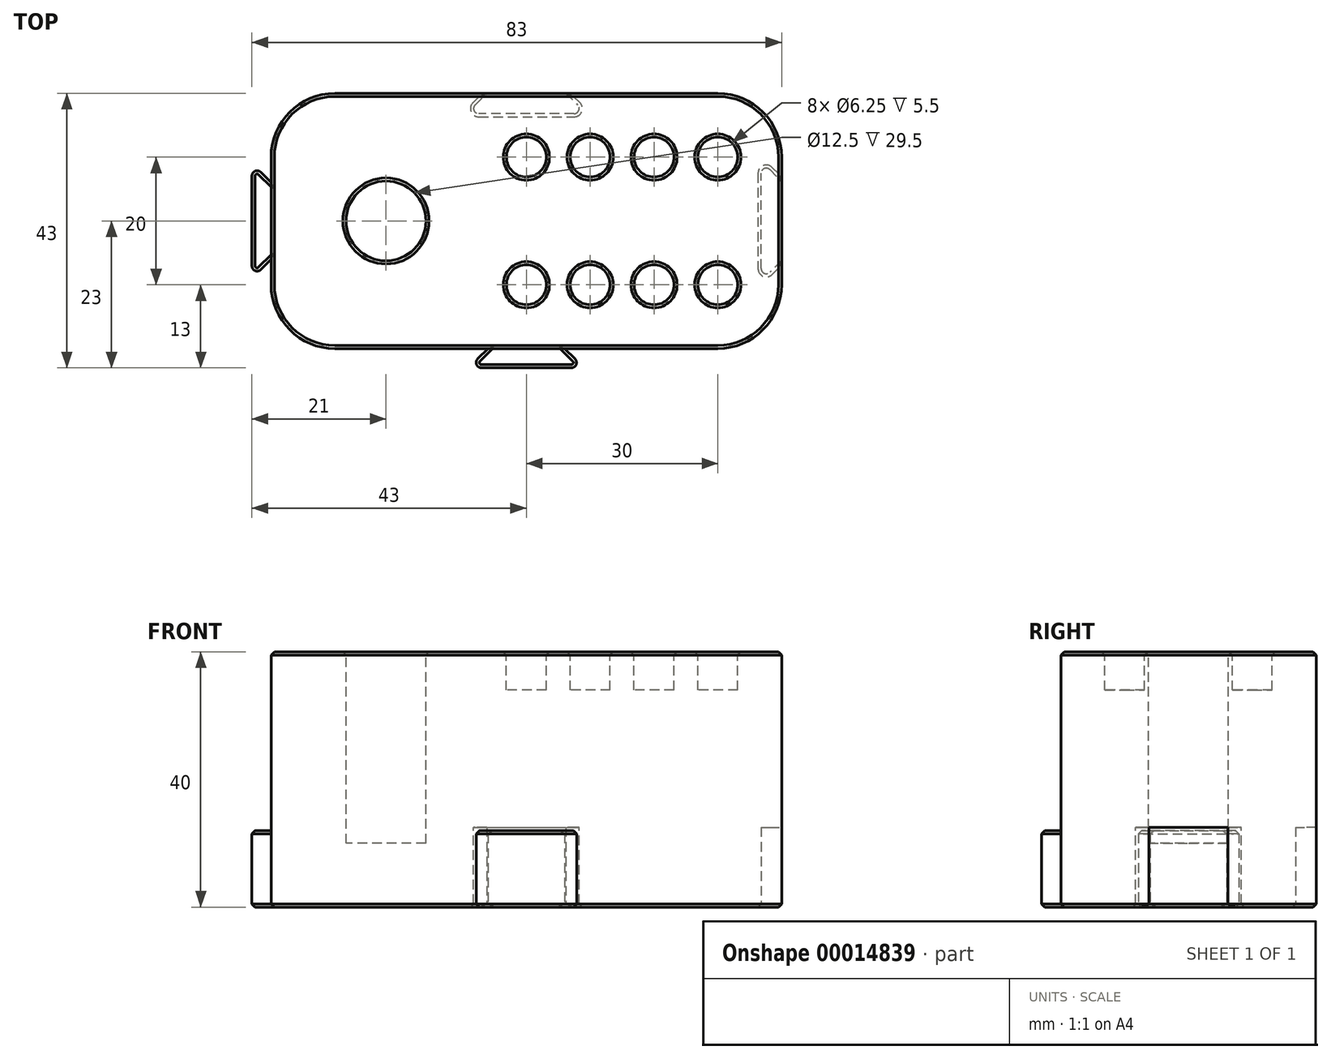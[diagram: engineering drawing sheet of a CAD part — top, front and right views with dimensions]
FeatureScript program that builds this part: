
annotation { "Feature Type Name" : "Feature", "Feature Type Description" : "" }
export const myFeature = defineFeature(function(context is Context, id is Id, definition is map)
    precondition{}
    {
        {
            var Q0;
            Q0=qCreatedBy(makeId("Top.planeOp"),FACE);
            var sketch = newSketch(context, id + "F0", { "sketchPlane" : qUnion([Q0])});
            skLineSegment(sketch, "E0.bottom", {"start": v(0, 0) * mm, "end": v(80, 0) * mm});
            skLineSegment(sketch, "E0.top", {"start": v(0, 40) * mm, "end": v(80, 40) * mm});
            skLineSegment(sketch, "E0.left", {"start": v(0, 0) * mm, "end": v(0, 40) * mm});
            skLineSegment(sketch, "E0.right", {"start": v(80, 0) * mm, "end": v(80, 40) * mm});
            skLineSegment(sketch, "E1", {"start": v(34, 0) * mm, "end": v(31, -3) * mm});
            skLineSegment(sketch, "E2", {"start": v(31, -3) * mm, "end": v(49, -3) * mm});
            skLineSegment(sketch, "E3", {"start": v(49, -3) * mm, "end": v(46, 0) * mm});
            skLineSegment(sketch, "E4", {"start": v(33.8, 40) * mm, "end": v(30.6, 36.8) * mm});
            skLineSegment(sketch, "E5", {"start": v(30.6, 36.8) * mm, "end": v(49.4, 36.8) * mm});
            skLineSegment(sketch, "E6", {"start": v(49.4, 36.8) * mm, "end": v(46.2, 40) * mm});
            skLineSegment(sketch, "E7", {"start": v(0, 26) * mm, "end": v(-3, 29) * mm});
            skLineSegment(sketch, "E8", {"start": v(-3, 29) * mm, "end": v(-3, 11) * mm});
            skLineSegment(sketch, "E9", {"start": v(-3, 11) * mm, "end": v(0, 14) * mm});
            skLineSegment(sketch, "E10", {"start": v(80, 26.2) * mm, "end": v(76.8, 29.4) * mm});
            skLineSegment(sketch, "E11", {"start": v(76.8, 29.4) * mm, "end": v(76.8, 10.6) * mm});
            skLineSegment(sketch, "E12", {"start": v(76.8, 10.6) * mm, "end": v(80, 13.8) * mm});
            skLineSegment(sketch, "E13", {"start": v(40, 0) * mm, "end": v(40, 40) * mm, "construction": true});
            skLineSegment(sketch, "E14", {"start": v(0, 20) * mm, "end": v(80, 20) * mm, "construction": true});
            skSolve(sketch);
        }
        {
            var Q0;
            {var subQ8=sQuery(id+"F0.wireOp",EDGE,"E4");Q0=makeQuery(id+"F0.imprint","IMPRINT",FACE,{"disambiguationData":[TD([[makeQuery(id+"F0.imprint","IMPRINT",EDGE,{"derivedFrom":subQ8}),-1.0]])]});}
            var Q1;
            {var subQ1=sQuery(id+"F0.wireOp",EDGE,"E10");Q1=makeQuery(id+"F0.imprint","IMPRINT",FACE,{"disambiguationData":[TD([[makeQuery(id+"F0.imprint","IMPRINT",EDGE,{"derivedFrom":subQ1}),1.0]])]});}
            var Q2;
            {var subQ1=sQuery(id+"F0.wireOp",EDGE,"E4");Q2=makeQuery(id+"F0.imprint","IMPRINT",FACE,{"disambiguationData":[TD([[makeQuery(id+"F0.imprint","IMPRINT",EDGE,{"derivedFrom":subQ1}),1.0]])]});}
            extrude(context, id + "F1", {"entities" : qUnion([Q0, Q1, Q2]), "depth" : 40 * mm});
        }
        {
            var Q0;
            {var subQ1=sQuery(id+"F0.wireOp",EDGE,"E10");Q0=makeQuery(id+"F0.imprint","IMPRINT",FACE,{"disambiguationData":[TD([[makeQuery(id+"F0.imprint","IMPRINT",EDGE,{"derivedFrom":subQ1}),1.0]])]});}
            var Q1;
            {var subQ1=sQuery(id+"F0.wireOp",EDGE,"E4");Q1=makeQuery(id+"F0.imprint","IMPRINT",FACE,{"disambiguationData":[TD([[makeQuery(id+"F0.imprint","IMPRINT",EDGE,{"derivedFrom":subQ1}),1.0]])]});}
            extrude(context, id + "F2", {"entities" : qUnion([Q0, Q1]), "operationType" : NewBodyOperationType.REMOVE, "depth" : 12.5 * mm});
        }
        {
            var Q0;
            {var subQ1=sQuery(id+"F0.wireOp",EDGE,"E1");Q0=makeQuery(id+"F0.imprint","IMPRINT",FACE,{"disambiguationData":[TD([[makeQuery(id+"F0.imprint","IMPRINT",EDGE,{"derivedFrom":subQ1}),1.0]])]});}
            var Q1;
            {var subQ1=sQuery(id+"F0.wireOp",EDGE,"E7");Q1=makeQuery(id+"F0.imprint","IMPRINT",FACE,{"disambiguationData":[TD([[makeQuery(id+"F0.imprint","IMPRINT",EDGE,{"derivedFrom":subQ1}),1.0]])]});}
            extrude(context, id + "F3", {"entities" : qUnion([Q0, Q1]), "operationType" : NewBodyOperationType.ADD, "depth" : 12 * mm});
        }
        {
            var Q0;
            Q0=makeQuery(id+"F2.boolean.opBoolean","COPY",EDGE,{"derivedFrom":makeQuery(id+"F2.opExtrude","SWEPT_EDGE",EDGE,{"disambiguationData":[OSD([sQuery(id+"F0.wireOp",EDGE,"E0.top"),sQuery(id+"F0.wireOp",EDGE,"E4")])]})});
            var Q1;
            Q1=makeQuery(id+"F2.boolean.opBoolean","COPY",EDGE,{"derivedFrom":makeQuery(id+"F2.opExtrude","SWEPT_EDGE",EDGE,{"disambiguationData":[OSD([sQuery(id+"F0.wireOp",EDGE,"E4"),sQuery(id+"F0.wireOp",EDGE,"E5")])]})});
            var Q2;
            Q2=makeQuery(id+"F2.boolean.opBoolean","COPY",EDGE,{"derivedFrom":makeQuery(id+"F2.opExtrude","SWEPT_EDGE",EDGE,{"disambiguationData":[OSD([sQuery(id+"F0.wireOp",EDGE,"E5"),sQuery(id+"F0.wireOp",EDGE,"E6")])]})});
            var Q3;
            Q3=makeQuery(id+"F2.boolean.opBoolean","COPY",EDGE,{"derivedFrom":makeQuery(id+"F2.opExtrude","SWEPT_EDGE",EDGE,{"disambiguationData":[OSD([sQuery(id+"F0.wireOp",EDGE,"E0.top"),sQuery(id+"F0.wireOp",EDGE,"E6")])]})});
            var Q4;
            Q4=makeQuery(id+"F3.opExtrude","SWEPT_EDGE",EDGE,{"disambiguationData":[OSD([sQuery(id+"F0.wireOp",EDGE,"E7"),sQuery(id+"F0.wireOp",EDGE,"E8")])]});
            var Q5;
            Q5=makeQuery(id+"F3.opExtrude","SWEPT_EDGE",EDGE,{"disambiguationData":[OSD([sQuery(id+"F0.wireOp",EDGE,"E8"),sQuery(id+"F0.wireOp",EDGE,"E9")])]});
            var Q6;
            Q6=makeQuery(id+"F3.opExtrude","SWEPT_EDGE",EDGE,{"disambiguationData":[OSD([sQuery(id+"F0.wireOp",EDGE,"E0.left"),sQuery(id+"F0.wireOp",EDGE,"E7")])]});
            var Q7;
            Q7=makeQuery(id+"F3.opExtrude","SWEPT_EDGE",EDGE,{"disambiguationData":[OSD([sQuery(id+"F0.wireOp",EDGE,"E0.left"),sQuery(id+"F0.wireOp",EDGE,"E9")])]});
            var Q8;
            Q8=makeQuery(id+"F3.opExtrude","SWEPT_EDGE",EDGE,{"disambiguationData":[OSD([sQuery(id+"F0.wireOp",EDGE,"E2"),sQuery(id+"F0.wireOp",EDGE,"E3")])]});
            var Q9;
            Q9=makeQuery(id+"F3.opExtrude","SWEPT_EDGE",EDGE,{"disambiguationData":[OSD([sQuery(id+"F0.wireOp",EDGE,"E1"),sQuery(id+"F0.wireOp",EDGE,"E2")])]});
            var Q10;
            Q10=makeQuery(id+"F3.opExtrude","SWEPT_EDGE",EDGE,{"disambiguationData":[OSD([sQuery(id+"F0.wireOp",EDGE,"E0.bottom"),sQuery(id+"F0.wireOp",EDGE,"E1")])]});
            var Q11;
            Q11=makeQuery(id+"F3.opExtrude","SWEPT_EDGE",EDGE,{"disambiguationData":[OSD([sQuery(id+"F0.wireOp",EDGE,"E0.bottom"),sQuery(id+"F0.wireOp",EDGE,"E3")])]});
            var Q12;
            Q12=makeQuery(id+"F2.boolean.opBoolean","COPY",EDGE,{"derivedFrom":makeQuery(id+"F2.opExtrude","SWEPT_EDGE",EDGE,{"disambiguationData":[OSD([sQuery(id+"F0.wireOp",EDGE,"E0.right"),sQuery(id+"F0.wireOp",EDGE,"E10")])]})});
            var Q13;
            Q13=makeQuery(id+"F2.boolean.opBoolean","COPY",EDGE,{"derivedFrom":makeQuery(id+"F2.opExtrude","SWEPT_EDGE",EDGE,{"disambiguationData":[OSD([sQuery(id+"F0.wireOp",EDGE,"E0.right"),sQuery(id+"F0.wireOp",EDGE,"E12")])]})});
            var Q14;
            Q14=makeQuery(id+"F2.boolean.opBoolean","COPY",EDGE,{"derivedFrom":makeQuery(id+"F2.opExtrude","SWEPT_EDGE",EDGE,{"disambiguationData":[OSD([sQuery(id+"F0.wireOp",EDGE,"E10"),sQuery(id+"F0.wireOp",EDGE,"E11")])]})});
            var Q15;
            Q15=makeQuery(id+"F2.boolean.opBoolean","COPY",EDGE,{"derivedFrom":makeQuery(id+"F2.opExtrude","SWEPT_EDGE",EDGE,{"disambiguationData":[OSD([sQuery(id+"F0.wireOp",EDGE,"E11"),sQuery(id+"F0.wireOp",EDGE,"E12")])]})});
            fillet(context, id + "F4", {"entities" : qUnion([Q0, Q1, Q2, Q3, Q4, Q5, Q6, Q7, Q8, Q9, Q10, Q11, Q12, Q13, Q14, Q15]), "radius" : .8 * mm, "tangentPropagation" : true, "allowEdgeOverflow" : false});
        }
        {
            var Q0;
            Q0=makeQuery(id+"F1.opExtrude","CAP_FACE",FACE,{"disambiguationData":[OSD([sQuery(id+"F0.wireOp",EDGE,"E0.bottom"),sQuery(id+"F0.wireOp",EDGE,"E0.top"),sQuery(id+"F0.wireOp",EDGE,"E0.left"),sQuery(id+"F0.wireOp",EDGE,"E0.right")])],"isStart":false});
            var sketch = newSketch(context, id + "F5", { "sketchPlane" : qUnion([Q0])});
            skCircle(sketch, "E15", {"center": v(18, 20) * mm, "radius": 6.25 * mm});
            skCircle(sketch, "E16", {"center": v(40, 30) * mm, "radius": 3.12 * mm});
            skCircle(sketch, "E17", {"center": v(40, 10) * mm, "radius": 3.12 * mm});
            skCircle(sketch, "E18", {"center": v(50, 30) * mm, "radius": 3.12 * mm});
            skCircle(sketch, "E19", {"center": v(60, 30) * mm, "radius": 3.12 * mm});
            skCircle(sketch, "E20", {"center": v(50, 10) * mm, "radius": 3.12 * mm});
            skCircle(sketch, "E21", {"center": v(60, 10) * mm, "radius": 3.12 * mm});
            skCircle(sketch, "E22", {"center": v(70, 10) * mm, "radius": 3.12 * mm});
            skCircle(sketch, "E23", {"center": v(70, 30) * mm, "radius": 3.12 * mm});
            skLineSegment(sketch, "E24", {"start": v(0, 20) * mm, "end": v(80, 20) * mm, "construction": true});
            skCircle(sketch, "E25", {"center": v(55, 20) * mm, "radius": 2 * mm});
            skSolve(sketch);
        }
        {
            var Q0;
            Q0=makeQuery(id+"F5.imprint","IMPRINT",FACE,{"disambiguationData":[TD([[makeQuery(id+"F5.imprint","IMPRINT",EDGE,{"derivedFrom":sQuery(id+"F5.wireOp",EDGE,"E15")}),1.0]])]});
            extrude(context, id + "F6", {"entities" : qUnion([Q0]), "operationType" : NewBodyOperationType.REMOVE, "oppositeDirection" : true, "depth" : 30 * mm});
        }
        {
            var Q0;
            Q0=makeQuery(id+"F5.imprint","IMPRINT",FACE,{"disambiguationData":[TD([[makeQuery(id+"F5.imprint","IMPRINT",EDGE,{"derivedFrom":sQuery(id+"F5.wireOp",EDGE,"E16")}),1.0]])]});
            var Q1;
            Q1=makeQuery(id+"F5.imprint","IMPRINT",FACE,{"disambiguationData":[TD([[makeQuery(id+"F5.imprint","IMPRINT",EDGE,{"derivedFrom":sQuery(id+"F5.wireOp",EDGE,"E18")}),1.0]])]});
            var Q2;
            Q2=makeQuery(id+"F5.imprint","IMPRINT",FACE,{"disambiguationData":[TD([[makeQuery(id+"F5.imprint","IMPRINT",EDGE,{"derivedFrom":sQuery(id+"F5.wireOp",EDGE,"E19")}),1.0]])]});
            var Q3;
            Q3=makeQuery(id+"F5.imprint","IMPRINT",FACE,{"disambiguationData":[TD([[makeQuery(id+"F5.imprint","IMPRINT",EDGE,{"derivedFrom":sQuery(id+"F5.wireOp",EDGE,"E23")}),1.0]])]});
            var Q4;
            Q4=makeQuery(id+"F5.imprint","IMPRINT",FACE,{"disambiguationData":[TD([[makeQuery(id+"F5.imprint","IMPRINT",EDGE,{"derivedFrom":sQuery(id+"F5.wireOp",EDGE,"E22")}),1.0]])]});
            var Q5;
            Q5=makeQuery(id+"F5.imprint","IMPRINT",FACE,{"disambiguationData":[TD([[makeQuery(id+"F5.imprint","IMPRINT",EDGE,{"derivedFrom":sQuery(id+"F5.wireOp",EDGE,"E21")}),1.0]])]});
            var Q6;
            Q6=makeQuery(id+"F5.imprint","IMPRINT",FACE,{"disambiguationData":[TD([[makeQuery(id+"F5.imprint","IMPRINT",EDGE,{"derivedFrom":sQuery(id+"F5.wireOp",EDGE,"E20")}),1.0]])]});
            var Q7;
            Q7=makeQuery(id+"F5.imprint","IMPRINT",FACE,{"disambiguationData":[TD([[makeQuery(id+"F5.imprint","IMPRINT",EDGE,{"derivedFrom":sQuery(id+"F5.wireOp",EDGE,"E17")}),1.0]])]});
            extrude(context, id + "F7", {"entities" : qUnion([Q0, Q1, Q2, Q3, Q4, Q5, Q6, Q7]), "operationType" : NewBodyOperationType.REMOVE, "oppositeDirection" : true, "depth" : 6 * mm});
        }
        {
            var Q0;
            Q0=makeQuery(id+"F1.opExtrude","SWEPT_EDGE",EDGE,{"disambiguationData":[OSD([sQuery(id+"F0.wireOp",EDGE,"E0.bottom"),sQuery(id+"F0.wireOp",EDGE,"E0.left")])]});
            var Q1;
            Q1=makeQuery(id+"F1.opExtrude","SWEPT_EDGE",EDGE,{"disambiguationData":[OSD([sQuery(id+"F0.wireOp",EDGE,"E0.top"),sQuery(id+"F0.wireOp",EDGE,"E0.left")])]});
            var Q2;
            Q2=makeQuery(id+"F1.opExtrude","SWEPT_EDGE",EDGE,{"disambiguationData":[OSD([sQuery(id+"F0.wireOp",EDGE,"E0.bottom"),sQuery(id+"F0.wireOp",EDGE,"E0.right")])]});
            var Q3;
            Q3=makeQuery(id+"F1.opExtrude","SWEPT_EDGE",EDGE,{"disambiguationData":[OSD([sQuery(id+"F0.wireOp",EDGE,"E0.top"),sQuery(id+"F0.wireOp",EDGE,"E0.right")])]});
            fillet(context, id + "F8", {"entities" : qUnion([Q0, Q1, Q2, Q3]), "radius" : 10 * mm, "tangentPropagation" : true, "allowEdgeOverflow" : false});
        }
        {
            var Q0;
            {var subQ0=sQuery(id+"F0.wireOp",EDGE,"E0.bottom");var subQ1=sQuery(id+"F0.wireOp",EDGE,"E0.left");Q0=makeQuery(id+"F3.boolean.opBoolean","MERGE",FACE,{"derivedFrom":[makeQuery(id+"F1.opExtrude","CAP_FACE",FACE,{"disambiguationData":[OSD([subQ0,sQuery(id+"F0.wireOp",EDGE,"E0.top"),subQ1,sQuery(id+"F0.wireOp",EDGE,"E0.right")])],"isStart":true}),makeQuery(id+"F3.opExtrude","CAP_FACE",FACE,{"disambiguationData":[OSD([subQ0,sQuery(id+"F0.wireOp",EDGE,"E1"),sQuery(id+"F0.wireOp",EDGE,"E2"),sQuery(id+"F0.wireOp",EDGE,"E3")])],"isStart":true}),makeQuery(id+"F3.opExtrude","CAP_FACE",FACE,{"disambiguationData":[OSD([subQ1,sQuery(id+"F0.wireOp",EDGE,"E7"),sQuery(id+"F0.wireOp",EDGE,"E8"),sQuery(id+"F0.wireOp",EDGE,"E9")])],"isStart":true})]});}
            chamfer(context, id + "F9", {"entities" : qUnion([Q0]), "width" : .5 * mm, "tangentPropagation" : true});
        }
        {
            var Q0;
            Q0=makeQuery(id+"F1.opExtrude","CAP_FACE",FACE,{"disambiguationData":[OSD([sQuery(id+"F0.wireOp",EDGE,"E0.bottom"),sQuery(id+"F0.wireOp",EDGE,"E0.top"),sQuery(id+"F0.wireOp",EDGE,"E0.left"),sQuery(id+"F0.wireOp",EDGE,"E0.right")])],"isStart":false});
            chamfer(context, id + "F10", {"entities" : qUnion([Q0]), "width" : .5 * mm, "tangentPropagation" : true});
        }
        {
            var Q0;
            Q0=makeQuery(id+"F3.opExtrude","CAP_EDGE",EDGE,{"disambiguationData":[OSD([sQuery(id+"F0.wireOp",EDGE,"E2")])],"isStart":false});
            var Q1;
            Q1=makeQuery(id+"F3.opExtrude","CAP_EDGE",EDGE,{"disambiguationData":[OSD([sQuery(id+"F0.wireOp",EDGE,"E8")])],"isStart":false});
            chamfer(context, id + "F11", {"entities" : qUnion([Q0, Q1]), "width" : .5 * mm, "tangentPropagation" : true});
        }
    });
